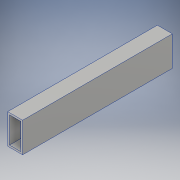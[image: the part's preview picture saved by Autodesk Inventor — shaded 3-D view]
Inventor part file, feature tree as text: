
AUTODESK INVENTOR PART (.ipt)
format: ipt  version: 2019 (Build 230136000, 136)  size: 106,496 bytes
history: native  units: in
note: dims shown in document units (in); Inventor stores cm internally (conversion verified against a paired STEP export)
features: extrude x1, sketch x1
ambient origin geometry x8: Origin, YZ Plane, XZ Plane, XY Plane, X Axis, Y Axis, Z Axis, Center Point
bodies: Solid1 (feature_tree)
feature tree (2):
  extrude  "Extrusion1"  [1 undecoded]
  sketch  "Sketch1"  dims[d4=0.0in]
note: 1 required parameter value undecoded (feature->parameter linkage not recoverable at this tier; creation-order binding heuristic only, values carry confidence <= 0.55)
